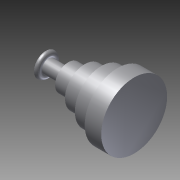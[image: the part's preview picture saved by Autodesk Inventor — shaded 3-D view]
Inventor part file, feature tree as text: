
AUTODESK INVENTOR PART (.ipt)
format: ipt  version: 2012 (Build 160160000, 160)  size: 119,808 bytes
history: native  units: mm
features: revolve x1, sketch x1
ambient origin geometry x8: Origin, YZ Plane, XZ Plane, XY Plane, X Axis, Y Axis, Z Axis, Center Point
bodies: Solid1 (feature_tree)
feature tree (2):
  revolve  "Revolution1"  [1 undecoded]
  sketch  "Sketch1"  dims[d2=5.0mm d3=5.0mm d4=5.0mm d5=5.0mm d7=2.0mm d8=2.0mm d9=2.0mm d10=2.0mm d11=2.0mm d12=2.0mm d13=90.0deg]
note: 1 required parameter value undecoded (feature->parameter linkage not recoverable at this tier; creation-order binding heuristic only, values carry confidence <= 0.55)
